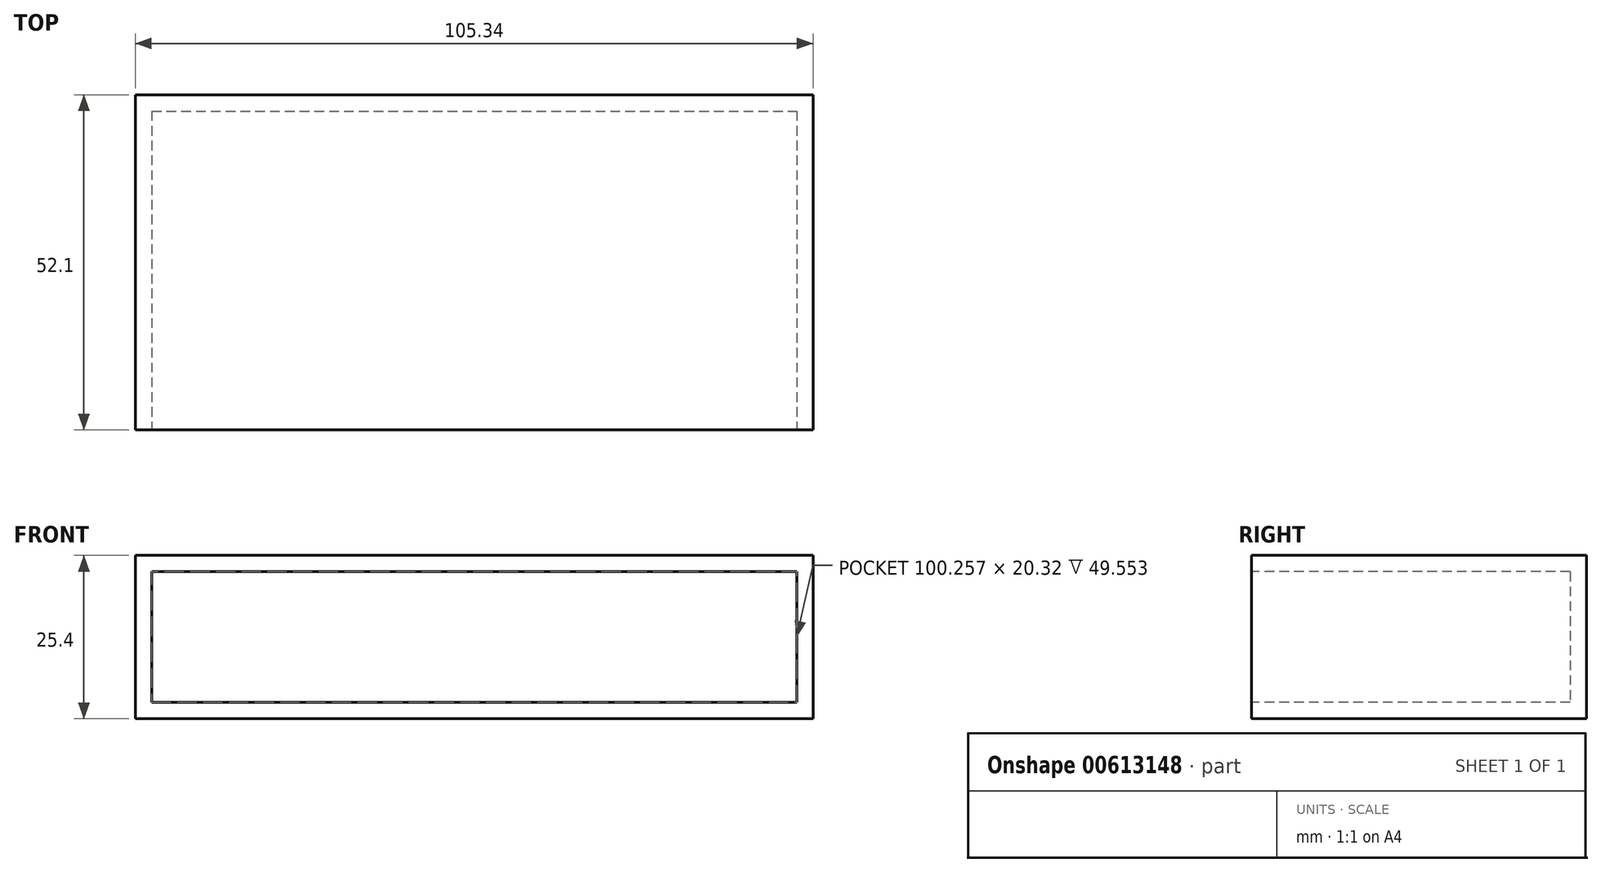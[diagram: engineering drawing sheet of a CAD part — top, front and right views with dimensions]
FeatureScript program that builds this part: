
annotation { "Feature Type Name" : "Feature", "Feature Type Description" : "" }
export const myFeature = defineFeature(function(context is Context, id is Id, definition is map)
    precondition{}
    {
        {
            var Q0;
            Q0=qCreatedBy(makeId("Top.planeOp"),FACE);
            var sketch = newSketch(context, id + "F0", { "sketchPlane" : qUnion([Q0])});
            skLineSegment(sketch, "E0.bottom", {"start": v(-46.77, 27.2) * mm, "end": v(58.57, 27.2) * mm});
            skLineSegment(sketch, "E0.top", {"start": v(-46.77, -24.9) * mm, "end": v(58.57, -24.9) * mm});
            skLineSegment(sketch, "E0.left", {"start": v(-46.77, 27.2) * mm, "end": v(-46.77, -24.9) * mm});
            skLineSegment(sketch, "E0.right", {"start": v(58.57, 27.2) * mm, "end": v(58.57, -24.9) * mm});
            skSolve(sketch);
        }
        {
            var Q0;
            Q0 = qSketchRegion(id + "F0", true);
            extrude(context, id + "F1", {"entities" : qUnion([Q0]), "depth" : 25.4 * mm, "offsetDistance" : 25.4 * mm});
        }
        {
            var Q0;
            Q0=makeQuery(id+"F1.opExtrude","CAP_FACE",FACE,{"disambiguationData":[OSD([sQuery(id+"F0.wireOp",EDGE,"E0.bottom"),sQuery(id+"F0.wireOp",EDGE,"E0.top"),sQuery(id+"F0.wireOp",EDGE,"E0.left"),sQuery(id+"F0.wireOp",EDGE,"E0.right")])],"isStart":false});
            var sketch = newSketch(context, id + "F2", { "sketchPlane" : qUnion([Q0])});
            skLineSegment(sketch, "E1.bottom", {"start": v(-46.77, 19.05) * mm, "end": v(45.04, 19.05) * mm});
            skLineSegment(sketch, "E1.top", {"start": v(-46.77, 0) * mm, "end": v(45.04, 0) * mm});
            skLineSegment(sketch, "E1.left", {"start": v(-46.77, 19.05) * mm, "end": v(-46.77, 0) * mm});
            skLineSegment(sketch, "E1.right", {"start": v(45.04, 19.05) * mm, "end": v(45.04, 0) * mm});
            skSolve(sketch);
        }
        {
            var Q0;
            Q0=makeQuery(id+"F1.opExtrude","SWEPT_FACE",FACE,{"disambiguationData":[OSD([sQuery(id+"F0.wireOp",EDGE,"E0.top")])]});
            shell(context, id + "F3", {"entities" : qUnion([Q0]), "thickness" : 2.54 * mm});
        }
    });
